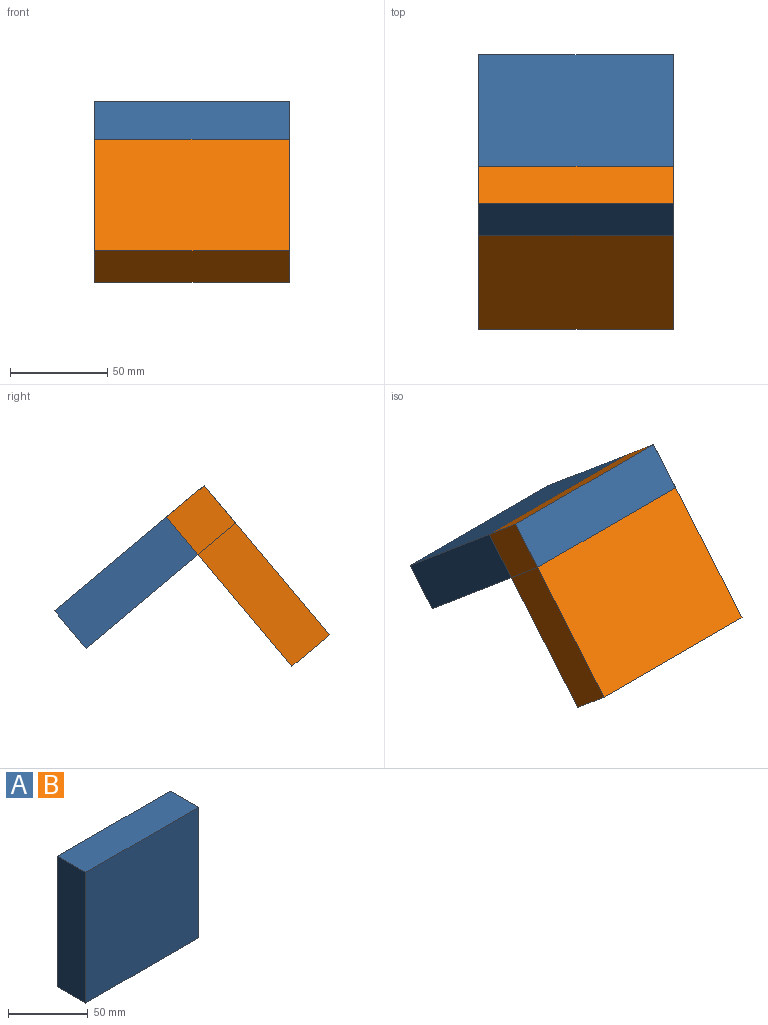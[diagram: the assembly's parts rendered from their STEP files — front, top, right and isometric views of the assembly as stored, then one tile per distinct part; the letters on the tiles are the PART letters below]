
ASSEMBLY  parts=2 mates=1
PART A: 6 faces, bbox 100x25x100 mm
  f0: plane 100x25mm, normal (0,0,1), area 2500mm2, adj f1,f3,f4,f5
  f1: plane 100x25mm, normal (-1,0,0), area 2500mm2, adj f0,f2,f4,f5
  f2: plane 100x25mm, normal (0,0,-1), area 2500mm2, adj f1,f3,f4,f5
  f3: plane 100x25mm, normal (1,0,0), area 2500mm2, adj f0,f2,f4,f5
  f4: plane 100x100mm, normal (0,-1,0), area 10000mm2, adj f0,f1,f2,f3
  f5: plane 100x100mm, normal (0,1,0), area 10000mm2, adj f0,f1,f2,f3
PART B: same geometry as A
PLACE A rot(axis=(0.39,-0.83,-0.39),100.3deg) t=(-29.63,29.98,97.48)mm
PLACE B rot(axis=(0.68,0.25,0.68),152deg) t=(-129.63,273.94,118.82)mm
MATE planar B.f2 <-> A.f0  axis (1,0,0) through (-129.63,162.63,-13.83)mm
